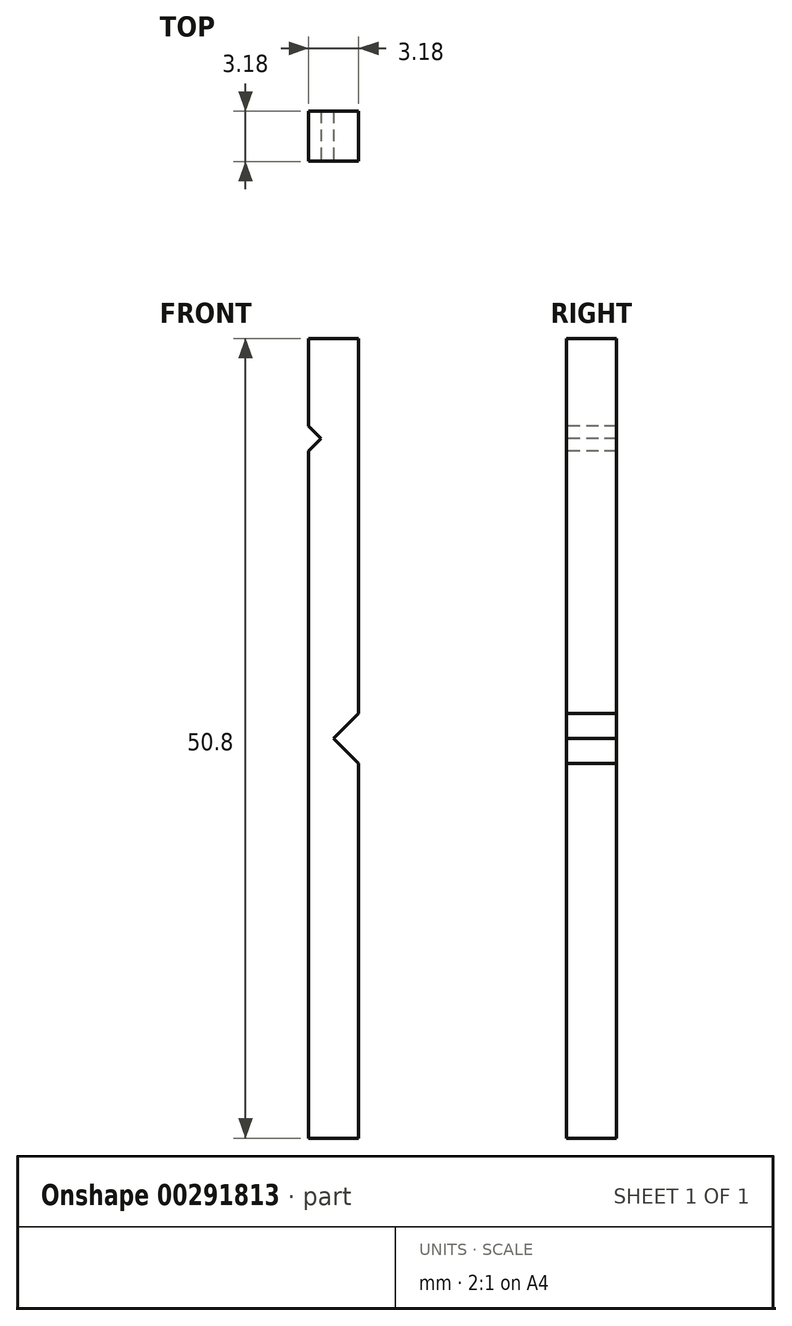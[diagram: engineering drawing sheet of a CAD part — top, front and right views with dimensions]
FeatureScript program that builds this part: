
annotation { "Feature Type Name" : "Feature", "Feature Type Description" : "" }
export const myFeature = defineFeature(function(context is Context, id is Id, definition is map)
    precondition{}
    {
        {
            var Q0;
            Q0=qCreatedBy(makeId("Front.planeOp"),FACE);
            var sketch = newSketch(context, id + "F0", { "sketchPlane" : qUnion([Q0])});
            skLineSegment(sketch, "E0.bottom", {"start": v(1.59, 25.4) * mm, "end": v(-1.59, 25.4) * mm});
            skLineSegment(sketch, "E0.top", {"start": v(1.59, -25.4) * mm, "end": v(-1.59, -25.4) * mm});
            skLineSegment(sketch, "E0.left", {"start": v(1.59, 25.4) * mm, "end": v(1.59, -25.4) * mm});
            skLineSegment(sketch, "E0.right", {"start": v(-1.59, 25.4) * mm, "end": v(-1.59, -25.4) * mm});
            skPoint(sketch, "E0.middle", {"position": v(0, 0) * mm});
            skSolve(sketch);
        }
        {
            var Q0;
            Q0 = qSketchRegion(id + "F0", true);
            extrude(context, id + "F1", {"entities" : qUnion([Q0]), "endBound" : BoundingType.SYMMETRIC, "depth" : 3.17 * mm});
        }
        {
            var Q0;
            Q0=makeQuery(id+"F1.opExtrude","CAP_FACE",FACE,{"disambiguationData":[OSD([sQuery(id+"F0.wireOp",EDGE,"E0.bottom"),sQuery(id+"F0.wireOp",EDGE,"E0.top"),sQuery(id+"F0.wireOp",EDGE,"E0.left"),sQuery(id+"F0.wireOp",EDGE,"E0.right")])],"isStart":false});
            var sketch = newSketch(context, id + "F2", { "sketchPlane" : qUnion([Q0])});
            skLineSegment(sketch, "E1", {"start": v(1.59, 0) * mm, "end": v(0, 0) * mm});
            skLineSegment(sketch, "E2", {"start": v(0, 0) * mm, "end": v(1.59, 1.59) * mm});
            skLineSegment(sketch, "E3", {"start": v(1.59, 1.59) * mm, "end": v(1.59, 0) * mm});
            skSolve(sketch);
        }
        {
            var Q0;
            Q0 = qSketchRegion(id + "F2", true);
            extrude(context, id + "F3", {"entities" : qUnion([Q0]), "operationType" : NewBodyOperationType.REMOVE, "endBound" : BoundingType.THROUGH_ALL, "oppositeDirection" : true, "depth" : 25.4 * mm});
        }
        {
            var Q0;
            Q0=makeQuery(id+"F1.opExtrude","CAP_FACE",FACE,{"disambiguationData":[OSD([sQuery(id+"F0.wireOp",EDGE,"E0.bottom"),sQuery(id+"F0.wireOp",EDGE,"E0.top"),sQuery(id+"F0.wireOp",EDGE,"E0.left"),sQuery(id+"F0.wireOp",EDGE,"E0.right")])],"isStart":false});
            var sketch = newSketch(context, id + "F4", { "sketchPlane" : qUnion([Q0])});
            skLineSegment(sketch, "E4", {"start": v(0, 0) * mm, "end": v(1.59, -1.59) * mm});
            skLineSegment(sketch, "E5", {"start": v(1.59, -1.59) * mm, "end": v(1.59, 0) * mm});
            skLineSegment(sketch, "E6", {"start": v(1.59, 0) * mm, "end": v(0, 0) * mm});
            skSolve(sketch);
        }
        {
            var Q0;
            Q0 = qSketchRegion(id + "F4", true);
            extrude(context, id + "F5", {"entities" : qUnion([Q0]), "operationType" : NewBodyOperationType.REMOVE, "endBound" : BoundingType.THROUGH_ALL, "oppositeDirection" : true, "depth" : 25.4 * mm});
        }
        {
            var Q0;
            Q0=makeQuery(id+"F1.opExtrude","CAP_FACE",FACE,{"disambiguationData":[OSD([sQuery(id+"F0.wireOp",EDGE,"E0.bottom"),sQuery(id+"F0.wireOp",EDGE,"E0.top"),sQuery(id+"F0.wireOp",EDGE,"E0.left"),sQuery(id+"F0.wireOp",EDGE,"E0.right")])],"isStart":false});
            var sketch = newSketch(context, id + "F6", { "sketchPlane" : qUnion([Q0])});
            skLineSegment(sketch, "E7", {"start": v(-0.8, 19.05) * mm, "end": v(-1.59, 19.84) * mm});
            skLineSegment(sketch, "E8", {"start": v(-1.59, 19.84) * mm, "end": v(-1.59, 18.26) * mm});
            skLineSegment(sketch, "E9", {"start": v(-1.59, 18.26) * mm, "end": v(-0.8, 19.05) * mm});
            skSolve(sketch);
        }
        {
            var Q0;
            Q0 = qSketchRegion(id + "F6", true);
            extrude(context, id + "F7", {"entities" : qUnion([Q0]), "operationType" : NewBodyOperationType.REMOVE, "endBound" : BoundingType.THROUGH_ALL, "oppositeDirection" : true, "depth" : 25.4 * mm});
        }
    });
